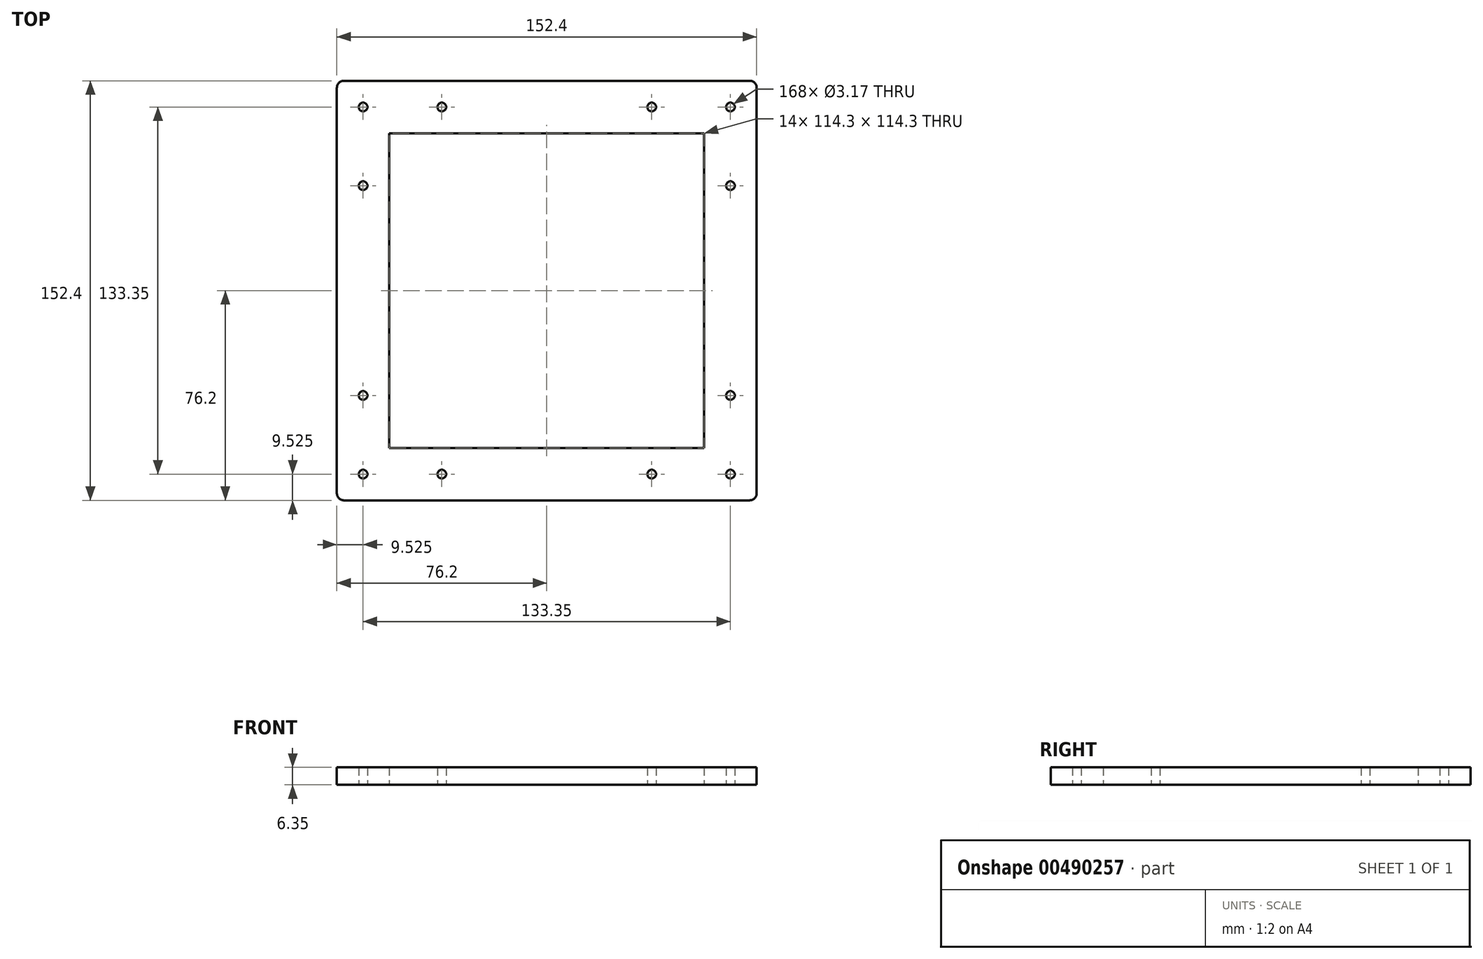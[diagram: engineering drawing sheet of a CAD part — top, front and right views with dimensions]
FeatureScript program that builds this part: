
annotation { "Feature Type Name" : "Feature", "Feature Type Description" : "" }
export const myFeature = defineFeature(function(context is Context, id is Id, definition is map)
    precondition{}
    {
        {
            var Q0;
            Q0=qCreatedBy(makeId("Top.planeOp"),FACE);
            var sketch = newSketch(context, id + "F0", { "sketchPlane" : qUnion([Q0])});
            skLineSegment(sketch, "E0.bottom", {"start": v(-76.2, 76.2) * mm, "end": v(76.2, 76.2) * mm});
            skLineSegment(sketch, "E0.top", {"start": v(-76.2, -76.2) * mm, "end": v(76.2, -76.2) * mm});
            skLineSegment(sketch, "E0.left", {"start": v(-76.2, 76.2) * mm, "end": v(-76.2, -76.2) * mm});
            skLineSegment(sketch, "E0.right", {"start": v(76.2, 76.2) * mm, "end": v(76.2, -76.2) * mm});
            skPoint(sketch, "E0.middle", {"position": v(0, 0) * mm});
            skLineSegment(sketch, "E1.bottom", {"start": v(-57.15, 57.15) * mm, "end": v(57.15, 57.15) * mm});
            skLineSegment(sketch, "E1.top", {"start": v(-57.15, -57.15) * mm, "end": v(57.15, -57.15) * mm});
            skLineSegment(sketch, "E1.left", {"start": v(-57.15, 57.15) * mm, "end": v(-57.15, -57.15) * mm});
            skLineSegment(sketch, "E1.right", {"start": v(57.15, 57.15) * mm, "end": v(57.15, -57.15) * mm});
            skPoint(sketch, "E2", {"position": v(-38.1, 66.67) * mm});
            skPoint(sketch, "E3", {"position": v(-66.67, 66.68) * mm});
            skLineSegment(sketch, "E4", {"start": v(-76.2, 76.2) * mm, "end": v(-57.15, 57.15) * mm});
            skPoint(sketch, "E5.MirrorP", {"position": v(-66.67, 38.1) * mm});
            skPoint(sketch, "E6.1.0", {"position": v(38.1, 66.67) * mm});
            skPoint(sketch, "E6.1.1", {"position": v(66.68, 66.67) * mm});
            skPoint(sketch, "E6.1.2", {"position": v(66.67, 38.1) * mm});
            skPoint(sketch, "E6.2.0", {"position": v(66.67, -38.1) * mm});
            skPoint(sketch, "E6.2.1", {"position": v(66.68, -66.68) * mm});
            skPoint(sketch, "E6.2.2", {"position": v(38.1, -66.67) * mm});
            skPoint(sketch, "E6.3.0", {"position": v(-38.1, -66.67) * mm});
            skPoint(sketch, "E6.3.1", {"position": v(-66.68, -66.68) * mm});
            skPoint(sketch, "E6.3.2", {"position": v(-66.67, -38.1) * mm});
            skLineSegment(sketch, "E6.anchor1", {"start": v(0, 0) * mm, "end": v(-66.67, 38.1) * mm, "construction": true});
            skLineSegment(sketch, "E6.anchor2", {"start": v(0, 0) * mm, "end": v(-38.1, -66.67) * mm, "construction": true});
            skSolve(sketch);
        }
        {
            var Q0;
            Q0=makeQuery(id+"F0.imprint","IMPRINT",FACE,{"disambiguationData":[TD([[makeQuery(id+"F0.imprint","IMPRINT",EDGE,{"derivedFrom":sQuery(id+"F0.wireOp",EDGE,"E0.bottom")}),-1.0]])]});
            extrude(context, id + "F1", {"entities" : qUnion([Q0]), "depth" : 6.35 * mm});
        }
        {
            var Q0;
            Q0=sQuery(id+"F0.wireOp",VERTEX,"E3");
            var Q1;
            Q1=sQuery(id+"F0.wireOp",VERTEX,"E2");
            var Q2;
            Q2=sQuery(id+"F0.wireOp",VERTEX,"E6.1.0");
            var Q3;
            Q3=sQuery(id+"F0.wireOp",VERTEX,"E6.1.1");
            var Q4;
            Q4=sQuery(id+"F0.wireOp",VERTEX,"E6.1.2");
            var Q5;
            Q5=sQuery(id+"F0.wireOp",VERTEX,"E6.2.0");
            var Q6;
            Q6=sQuery(id+"F0.wireOp",VERTEX,"E6.2.1");
            var Q7;
            Q7=sQuery(id+"F0.wireOp",VERTEX,"E6.2.2");
            var Q8;
            Q8=sQuery(id+"F0.wireOp",VERTEX,"E6.3.0");
            var Q9;
            Q9=sQuery(id+"F0.wireOp",VERTEX,"E6.3.1");
            var Q10;
            Q10=sQuery(id+"F0.wireOp",VERTEX,"E6.3.2");
            var Q11;
            Q11=sQuery(id+"F0.wireOp",VERTEX,"E5.MirrorP");
            var Q12;
            Q12=makeQuery(id+"F1.opExtrude","SWEPT_BODY",BODY,{"disambiguationData":[OSD([sQuery(id+"F0.wireOp",EDGE,"E0.bottom"),sQuery(id+"F0.wireOp",EDGE,"E0.top"),sQuery(id+"F0.wireOp",EDGE,"E0.left"),sQuery(id+"F0.wireOp",EDGE,"E0.right"),sQuery(id+"F0.wireOp",EDGE,"E1.bottom"),sQuery(id+"F0.wireOp",EDGE,"E1.top"),sQuery(id+"F0.wireOp",EDGE,"E1.left"),sQuery(id+"F0.wireOp",EDGE,"E1.right")])]});
            hole(context, id + "F2", {"style" : HoleStyle.SIMPLE, "endStyle" : HoleEndStyle.THROUGH, "oppositeDirection" : true, "holeDiameter" : 3.17 * mm, "isTappedThrough" : true, "tappedDepth" : 12.7 * mm, "tapClearance" : 3, "locations" : qUnion([Q0, Q1, Q2, Q3, Q4, Q5, Q6, Q7, Q8, Q9, Q10, Q11]), "scope" : qUnion([Q12])});
        }
        {
            var Q0;
            Q0=makeQuery(id+"F1.opExtrude","SWEPT_EDGE",EDGE,{"disambiguationData":[OSD([sQuery(id+"F0.wireOp",EDGE,"E0.top"),sQuery(id+"F0.wireOp",EDGE,"E0.left")])]});
            var Q1;
            Q1=makeQuery(id+"F1.opExtrude","SWEPT_EDGE",EDGE,{"disambiguationData":[OSD([sQuery(id+"F0.wireOp",EDGE,"E0.top"),sQuery(id+"F0.wireOp",EDGE,"E0.right")])]});
            var Q2;
            Q2=makeQuery(id+"F1.opExtrude","SWEPT_EDGE",EDGE,{"disambiguationData":[OSD([sQuery(id+"F0.wireOp",EDGE,"E0.bottom"),sQuery(id+"F0.wireOp",EDGE,"E0.right")])]});
            var Q3;
            Q3=makeQuery(id+"F1.opExtrude","SWEPT_EDGE",EDGE,{"disambiguationData":[OSD([sQuery(id+"F0.wireOp",EDGE,"E0.bottom"),sQuery(id+"F0.wireOp",EDGE,"E0.left")])]});
            fillet(context, id + "F3", {"entities" : qUnion([Q0, Q1, Q2, Q3]), "radius" : 2.54 * mm, "tangentPropagation" : true, "allowEdgeOverflow" : false});
        }
    });
